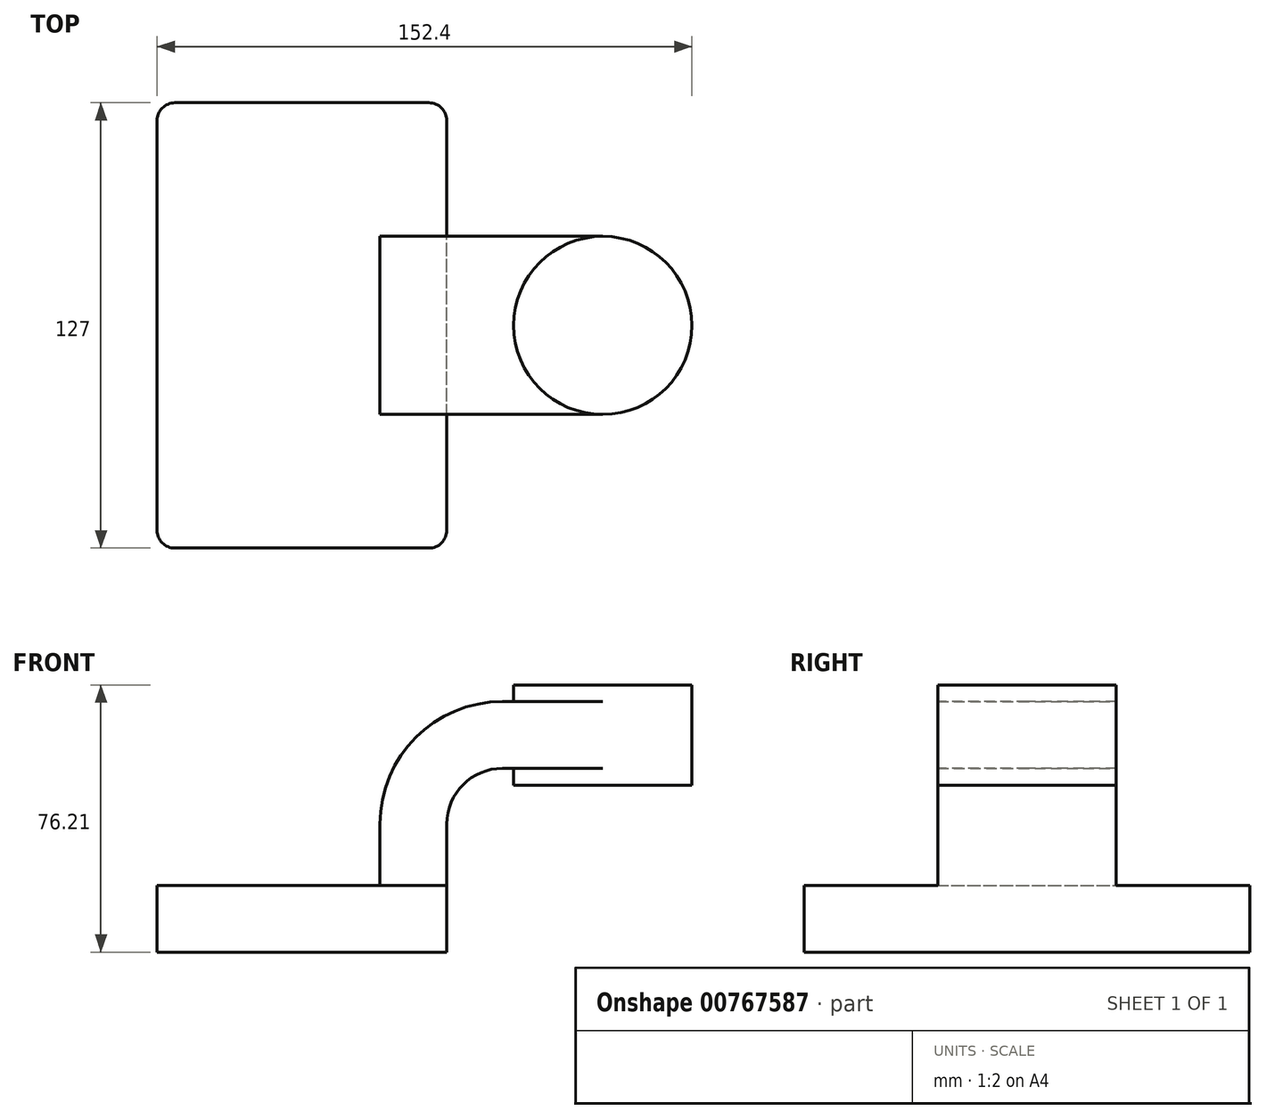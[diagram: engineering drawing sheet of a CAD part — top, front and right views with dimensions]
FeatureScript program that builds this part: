
annotation { "Feature Type Name" : "Feature", "Feature Type Description" : "" }
export const myFeature = defineFeature(function(context is Context, id is Id, definition is map)
    precondition{}
    {
        {
            var Q0;
            Q0=qCreatedBy(makeId("Front.planeOp"),FACE);
            var sketch = newSketch(context, id + "F0", { "sketchPlane" : qUnion([Q0])});
            skLineSegment(sketch, "E0.bottom", {"start": v(41.28, -9.53) * mm, "end": v(-41.28, -9.53) * mm});
            skLineSegment(sketch, "E0.top", {"start": v(41.28, 9.52) * mm, "end": v(-41.28, 9.52) * mm});
            skLineSegment(sketch, "E0.left", {"start": v(41.28, -9.53) * mm, "end": v(41.28, 9.52) * mm});
            skLineSegment(sketch, "E0.right", {"start": v(-41.28, -9.53) * mm, "end": v(-41.28, 9.52) * mm});
            skPoint(sketch, "E0.middle", {"position": v(0, 0) * mm});
            skLineSegment(sketch, "E1.bottom", {"start": v(111.12, 38.1) * mm, "end": v(60.32, 38.1) * mm});
            skLineSegment(sketch, "E1.top", {"start": v(111.12, 66.68) * mm, "end": v(60.32, 66.67) * mm});
            skLineSegment(sketch, "E1.left", {"start": v(111.12, 38.1) * mm, "end": v(111.12, 66.67) * mm});
            skLineSegment(sketch, "E1.right", {"start": v(60.32, 38.1) * mm, "end": v(60.32, 66.67) * mm});
            skPoint(sketch, "E1.middle", {"position": v(85.72, 52.39) * mm});
            skLineSegment(sketch, "E2", {"start": v(41.28, 9.52) * mm, "end": v(41.28, 27) * mm});
            skPoint(sketch, "E3.startSnap0", {"position": v(85.72, 38.1) * mm});
            skArc(sketch, "E4", {"start": v(41.28, 27) * mm, "mid": v(45.92, 38.23) * mm, "end": v(57.15, 42.88) * mm});
            skLineSegment(sketch, "E5", {"start": v(57.15, 42.88) * mm, "end": v(85.72, 42.88) * mm});
            skLineSegment(sketch, "E6.0", {"start": v(57.15, 61.93) * mm, "end": v(85.72, 61.93) * mm});
            skArc(sketch, "E6.1", {"start": v(22.23, 27) * mm, "mid": v(32.45, 51.7) * mm, "end": v(57.15, 61.93) * mm});
            skLineSegment(sketch, "E6.2", {"start": v(22.23, 9.52) * mm, "end": v(22.23, 27) * mm});
            skLineSegment(sketch, "E7", {"start": v(85.72, 38.1) * mm, "end": v(85.72, 66.68) * mm});
            skFitSpline(sketch, "E8", {"points": [v(-41.28, 9.52) * mm, v(57.15, 61.93) * mm], "startDerivative": vector(6.2, 76.71) * mm, "endDerivative": vector(132.24, -9.38) * mm});
            skSolve(sketch);
        }
        {
            var Q0;
            Q0=makeQuery(id+"F0.imprint","IMPRINT",FACE,{"disambiguationData":[TD([[makeQuery(id+"F0.imprint","IMPRINT",EDGE,{"derivedFrom":sQuery(id+"F0.wireOp",EDGE,"E0.bottom")}),-1.0]])]});
            extrude(context, id + "F1", {"entities" : qUnion([Q0]), "endBound" : BoundingType.SYMMETRIC, "depth" : 127 * mm, "offsetDistance" : 25.4 * mm});
        }
        {
            var Q0;
            {var subQ1=sQuery(id+"F0.wireOp",EDGE,"E2");Q0=makeQuery(id+"F0.imprint","IMPRINT",FACE,{"disambiguationData":[TD([[makeQuery(id+"F0.imprint","IMPRINT",EDGE,{"derivedFrom":subQ1}),1.0]])]});}
            var Q1;
            {var subQ0=sQuery(id+"F0.wireOp",EDGE,"E5");var subQ1=sQuery(id+"F0.wireOp",EDGE,"E1.right");var subQ2=makeQuery(id+"F0.imprint","INTERSECT",VERTEX,{"derivedFrom":[subQ1,subQ0]});Q1=makeQuery(id+"F0.imprint","IMPRINT",FACE,{"disambiguationData":[TD([[makeQuery(id+"F0.imprint","IMPRINT",EDGE,{"disambiguationData":[TD([[subQ2,-1.0]])],"derivedFrom":subQ1}),-1.0]])]});}
            extrude(context, id + "F2", {"entities" : qUnion([Q0, Q1]), "operationType" : NewBodyOperationType.ADD, "endBound" : BoundingType.SYMMETRIC, "depth" : 50.8 * mm, "offsetDistance" : 25.4 * mm});
        }
        {
            var Q0;
            Q0=makeQuery(id+"F0.imprint","IMPRINT",FACE,{"disambiguationData":[TD([[makeQuery(id+"F0.imprint","IMPRINT",EDGE,{"derivedFrom":sQuery(id+"F0.wireOp",EDGE,"E6.1")}),1.0]])]});
            extrude(context, id + "F3", {"entities" : qUnion([Q0]), "operationType" : NewBodyOperationType.ADD, "endBound" : BoundingType.SYMMETRIC, "depth" : 15.88 * mm, "offsetDistance" : 25.4 * mm});
        }
        {
            var Q0;
            {var subQ4=sQuery(id+"F0.wireOp",EDGE,"E1.left");Q0=makeQuery(id+"F0.imprint","IMPRINT",FACE,{"disambiguationData":[TD([[makeQuery(id+"F0.imprint","IMPRINT",EDGE,{"derivedFrom":subQ4}),1.0]])]});}
            var Q1;
            Q1=sQuery(id+"F0.wireOp",EDGE,"E7");
            revolve(context, id + "F4", {"operationType" : NewBodyOperationType.ADD, "surfaceOperationType" : NewSurfaceOperationType.NEW, "entities" : qUnion([Q0]), "axis" : qUnion([Q1]), "revolveType" : RevolveType.FULL});
        }
        {
            var Q0;
            Q0=makeQuery(id+"F1.opExtrude","CAP_EDGE",EDGE,{"disambiguationData":[OSD([sQuery(id+"F0.wireOp",EDGE,"E0.left")])],"isStart":false});
            var Q1;
            Q1=makeQuery(id+"F1.opExtrude","CAP_EDGE",EDGE,{"disambiguationData":[OSD([sQuery(id+"F0.wireOp",EDGE,"E0.right")])],"isStart":false});
            var Q2;
            Q2=makeQuery(id+"F1.opExtrude","CAP_EDGE",EDGE,{"disambiguationData":[OSD([sQuery(id+"F0.wireOp",EDGE,"E0.left")])],"isStart":true});
            var Q3;
            Q3=makeQuery(id+"F1.opExtrude","CAP_EDGE",EDGE,{"disambiguationData":[OSD([sQuery(id+"F0.wireOp",EDGE,"E0.right")])],"isStart":true});
            fillet(context, id + "F5", {"entities" : qUnion([Q0, Q1, Q2, Q3]), "radius" : 5.08 * mm, "tangentPropagation" : true, "allowEdgeOverflow" : false});
        }
    });
